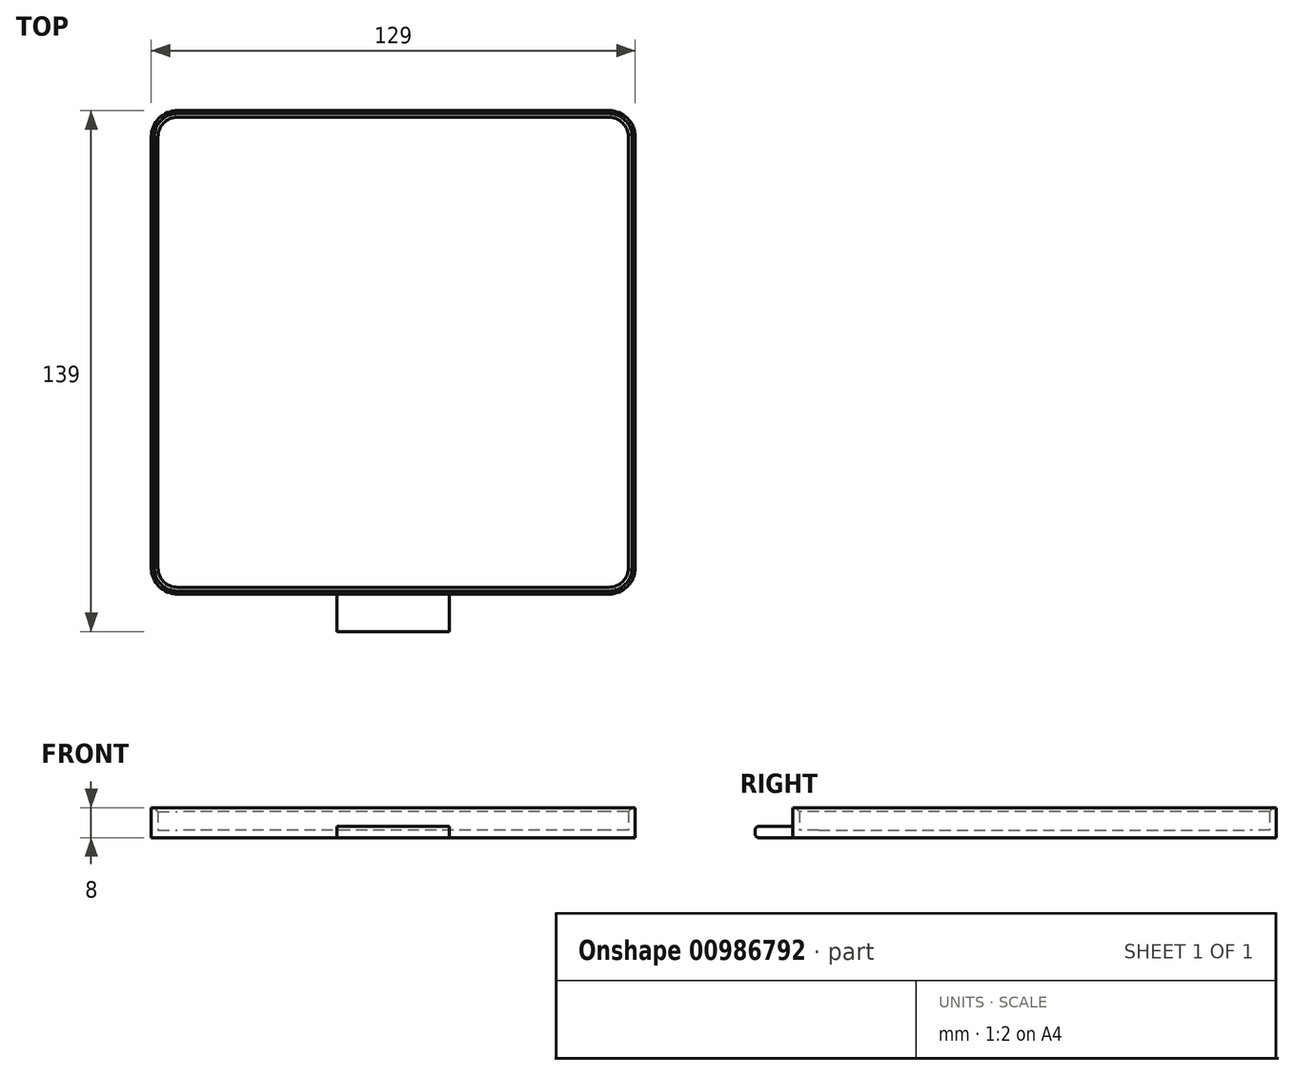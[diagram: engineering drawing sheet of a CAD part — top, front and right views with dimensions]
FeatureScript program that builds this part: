
annotation { "Feature Type Name" : "Feature", "Feature Type Description" : "" }
export const myFeature = defineFeature(function(context is Context, id is Id, definition is map)
    precondition{}
    {
        {
            var Q0;
            Q0=qCreatedBy(makeId("Top.planeOp"),FACE);
            var sketch = newSketch(context, id + "F0", { "sketchPlane" : qUnion([Q0])});
            skLineSegment(sketch, "E0.bottom", {"start": v(57.5, -64.5) * mm, "end": v(-57.5, -64.5) * mm});
            skLineSegment(sketch, "E0.top", {"start": v(57.5, 64.5) * mm, "end": v(-57.5, 64.5) * mm});
            skLineSegment(sketch, "E0.left", {"start": v(64.5, -57.5) * mm, "end": v(64.5, 57.5) * mm});
            skLineSegment(sketch, "E0.right", {"start": v(-64.5, -57.5) * mm, "end": v(-64.5, 57.5) * mm});
            skPoint(sketch, "E0.middle", {"position": v(0, 0) * mm});
            skPoint(sketch, "E1.visualSharp", {"position": v(-64.5, -64.5) * mm});
            skArc(sketch, "E1.filletArc", {"start": v(-64.5, -57.5) * mm, "mid": v(-62.45, -62.45) * mm, "end": v(-57.5, -64.5) * mm});
            skPoint(sketch, "E2.visualSharp", {"position": v(-64.5, 64.5) * mm});
            skArc(sketch, "E2.filletArc", {"start": v(-57.5, 64.5) * mm, "mid": v(-62.45, 62.45) * mm, "end": v(-64.5, 57.5) * mm});
            skPoint(sketch, "E3.visualSharp", {"position": v(64.5, 64.5) * mm});
            skArc(sketch, "E3.filletArc", {"start": v(64.5, 57.5) * mm, "mid": v(62.45, 62.45) * mm, "end": v(57.5, 64.5) * mm});
            skPoint(sketch, "E4.visualSharp", {"position": v(64.5, -64.5) * mm});
            skArc(sketch, "E4.filletArc", {"start": v(57.5, -64.5) * mm, "mid": v(62.45, -62.45) * mm, "end": v(64.5, -57.5) * mm});
            skArc(sketch, "E5.0", {"start": v(-62.7, -57.5) * mm, "mid": v(-61.18, -61.18) * mm, "end": v(-57.5, -62.7) * mm});
            skLineSegment(sketch, "E5.1", {"start": v(57.5, -62.7) * mm, "end": v(-57.5, -62.7) * mm});
            skLineSegment(sketch, "E5.2", {"start": v(-62.7, -57.5) * mm, "end": v(-62.7, 57.5) * mm});
            skArc(sketch, "E5.3", {"start": v(57.5, -62.7) * mm, "mid": v(61.18, -61.18) * mm, "end": v(62.7, -57.5) * mm});
            skArc(sketch, "E5.4", {"start": v(-57.5, 62.7) * mm, "mid": v(-61.18, 61.18) * mm, "end": v(-62.7, 57.5) * mm});
            skLineSegment(sketch, "E5.5", {"start": v(57.5, 62.7) * mm, "end": v(-57.5, 62.7) * mm});
            skArc(sketch, "E5.6", {"start": v(62.7, 57.5) * mm, "mid": v(61.18, 61.18) * mm, "end": v(57.5, 62.7) * mm});
            skLineSegment(sketch, "E5.7", {"start": v(62.7, -57.5) * mm, "end": v(62.7, 57.5) * mm});
            skSolve(sketch);
        }
        {
            var Q0;
            Q0=makeQuery(id+"F0.imprint","IMPRINT",FACE,{"disambiguationData":[TD([[makeQuery(id+"F0.imprint","IMPRINT",EDGE,{"derivedFrom":sQuery(id+"F0.wireOp",EDGE,"E0.bottom")}),-1.0]])]});
            extrude(context, id + "F1", {"entities" : qUnion([Q0]), "depth" : 8 * mm, "offsetDistance" : 25 * mm});
        }
        {
            var Q0;
            Q0=makeQuery(id+"F0.imprint","IMPRINT",FACE,{"disambiguationData":[TD([[makeQuery(id+"F0.imprint","IMPRINT",EDGE,{"derivedFrom":sQuery(id+"F0.wireOp",EDGE,"E5.0")}),1.0]])]});
            extrude(context, id + "F2", {"entities" : qUnion([Q0]), "operationType" : NewBodyOperationType.ADD, "depth" : 2 * mm, "offsetDistance" : 25 * mm});
        }
        {
            var Q0;
            Q0=makeQuery(id+"F1.opExtrude","SWEPT_FACE",FACE,{"disambiguationData":[OSD([sQuery(id+"F0.wireOp",EDGE,"E0.bottom")])]});
            var sketch = newSketch(context, id + "F3", { "sketchPlane" : qUnion([Q0])});
            skLineSegment(sketch, "E6.bottom", {"start": v(-15, 0) * mm, "end": v(15, 0) * mm});
            skLineSegment(sketch, "E6.top", {"start": v(-15, 3) * mm, "end": v(15, 3) * mm});
            skLineSegment(sketch, "E6.left", {"start": v(-15, 0) * mm, "end": v(-15, 3) * mm});
            skLineSegment(sketch, "E6.right", {"start": v(15, 0) * mm, "end": v(15, 3) * mm});
            skSolve(sketch);
        }
        {
            var Q0;
            Q0=makeQuery(id+"F3.imprint","IMPRINT",FACE,{"disambiguationData":[TD([[makeQuery(id+"F3.imprint","IMPRINT",EDGE,{"derivedFrom":sQuery(id+"F3.wireOp",EDGE,"E6.bottom")}),-1.0]])]});
            extrude(context, id + "F4", {"entities" : qUnion([Q0]), "operationType" : NewBodyOperationType.ADD, "depth" : 10 * mm, "offsetDistance" : 25 * mm});
        }
        {
            var Q0;
            Q0=makeQuery(id+"F4.opExtrude","CAP_EDGE",EDGE,{"disambiguationData":[OSD([sQuery(id+"F3.wireOp",EDGE,"E6.bottom")])],"isStart":false});
            var Q1;
            Q1=makeQuery(id+"F4.opExtrude","CAP_EDGE",EDGE,{"disambiguationData":[OSD([sQuery(id+"F3.wireOp",EDGE,"E6.top")])],"isStart":false});
            fillet(context, id + "F5", {"entities" : qUnion([Q0, Q1]), "radius" : 1 * mm, "tangentPropagation" : true, "allowEdgeOverflow" : false});
        }
        {
            var Q0;
            Q0=makeQuery(id+"F1.opExtrude","CAP_EDGE",EDGE,{"disambiguationData":[OSD([sQuery(id+"F0.wireOp",EDGE,"E5.5")])],"isStart":false});
            var Q1;
            Q1=makeQuery(id+"F1.opExtrude","CAP_EDGE",EDGE,{"disambiguationData":[OSD([sQuery(id+"F0.wireOp",EDGE,"E5.4")])],"isStart":false});
            var Q2;
            Q2=makeQuery(id+"F1.opExtrude","CAP_EDGE",EDGE,{"disambiguationData":[OSD([sQuery(id+"F0.wireOp",EDGE,"E5.2")])],"isStart":false});
            var Q3;
            Q3=makeQuery(id+"F1.opExtrude","CAP_EDGE",EDGE,{"disambiguationData":[OSD([sQuery(id+"F0.wireOp",EDGE,"E5.0")])],"isStart":false});
            var Q4;
            Q4=makeQuery(id+"F1.opExtrude","CAP_EDGE",EDGE,{"disambiguationData":[OSD([sQuery(id+"F0.wireOp",EDGE,"E5.1")])],"isStart":false});
            var Q5;
            Q5=makeQuery(id+"F1.opExtrude","CAP_EDGE",EDGE,{"disambiguationData":[OSD([sQuery(id+"F0.wireOp",EDGE,"E5.3")])],"isStart":false});
            var Q6;
            Q6=makeQuery(id+"F1.opExtrude","CAP_EDGE",EDGE,{"disambiguationData":[OSD([sQuery(id+"F0.wireOp",EDGE,"E5.7")])],"isStart":false});
            var Q7;
            Q7=makeQuery(id+"F1.opExtrude","CAP_EDGE",EDGE,{"disambiguationData":[OSD([sQuery(id+"F0.wireOp",EDGE,"E5.6")])],"isStart":false});
            chamfer(context, id + "F6", {"entities" : qUnion([Q0, Q1, Q2, Q3, Q4, Q5, Q6, Q7]), "width" : 1 * mm, "tangentPropagation" : true});
        }
    });
